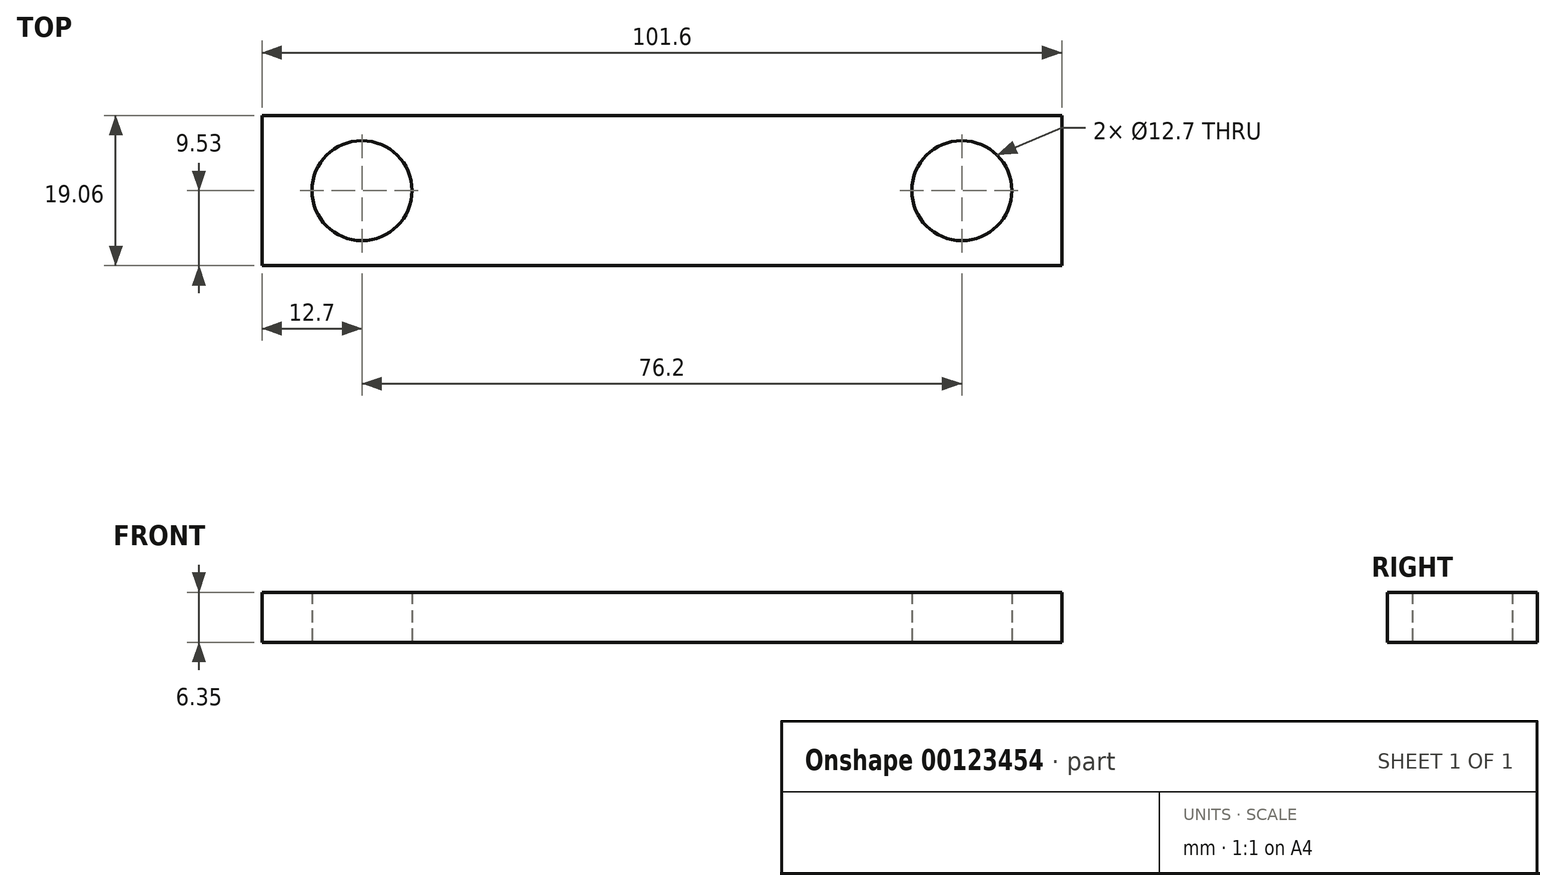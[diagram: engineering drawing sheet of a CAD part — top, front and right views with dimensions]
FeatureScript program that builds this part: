
annotation { "Feature Type Name" : "Feature", "Feature Type Description" : "" }
export const myFeature = defineFeature(function(context is Context, id is Id, definition is map)
    precondition{}
    {
        {
            var Q0;
            Q0=qCreatedBy(makeId("Top.planeOp"),FACE);
            var sketch = newSketch(context, id + "F0", { "sketchPlane" : qUnion([Q0])});
            skLineSegment(sketch, "E0.bottom", {"start": v(50.8, -9.53) * mm, "end": v(-50.8, -9.52) * mm});
            skLineSegment(sketch, "E0.top", {"start": v(50.8, 9.52) * mm, "end": v(-50.8, 9.53) * mm});
            skLineSegment(sketch, "E0.left", {"start": v(50.8, -9.53) * mm, "end": v(50.8, 9.52) * mm});
            skLineSegment(sketch, "E0.right", {"start": v(-50.8, -9.52) * mm, "end": v(-50.8, 9.52) * mm});
            skPoint(sketch, "E0.middle", {"position": v(0, 0) * mm});
            skLineSegment(sketch, "E1", {"start": v(0, 0) * mm, "end": v(50.8, 0) * mm, "construction": true});
            skCircle(sketch, "E2", {"center": v(38.1, 0) * mm, "radius": 6.35 * mm});
            skCircle(sketch, "E3.MirrorC", {"center": v(-38.1, 0) * mm, "radius": 6.35 * mm});
            skSolve(sketch);
        }
        {
            var Q0;
            Q0 = qSketchRegion(id + "F0", true);
            extrude(context, id + "F1", {"entities" : qUnion([Q0]), "depth" : 6.35 * mm});
        }
    });
